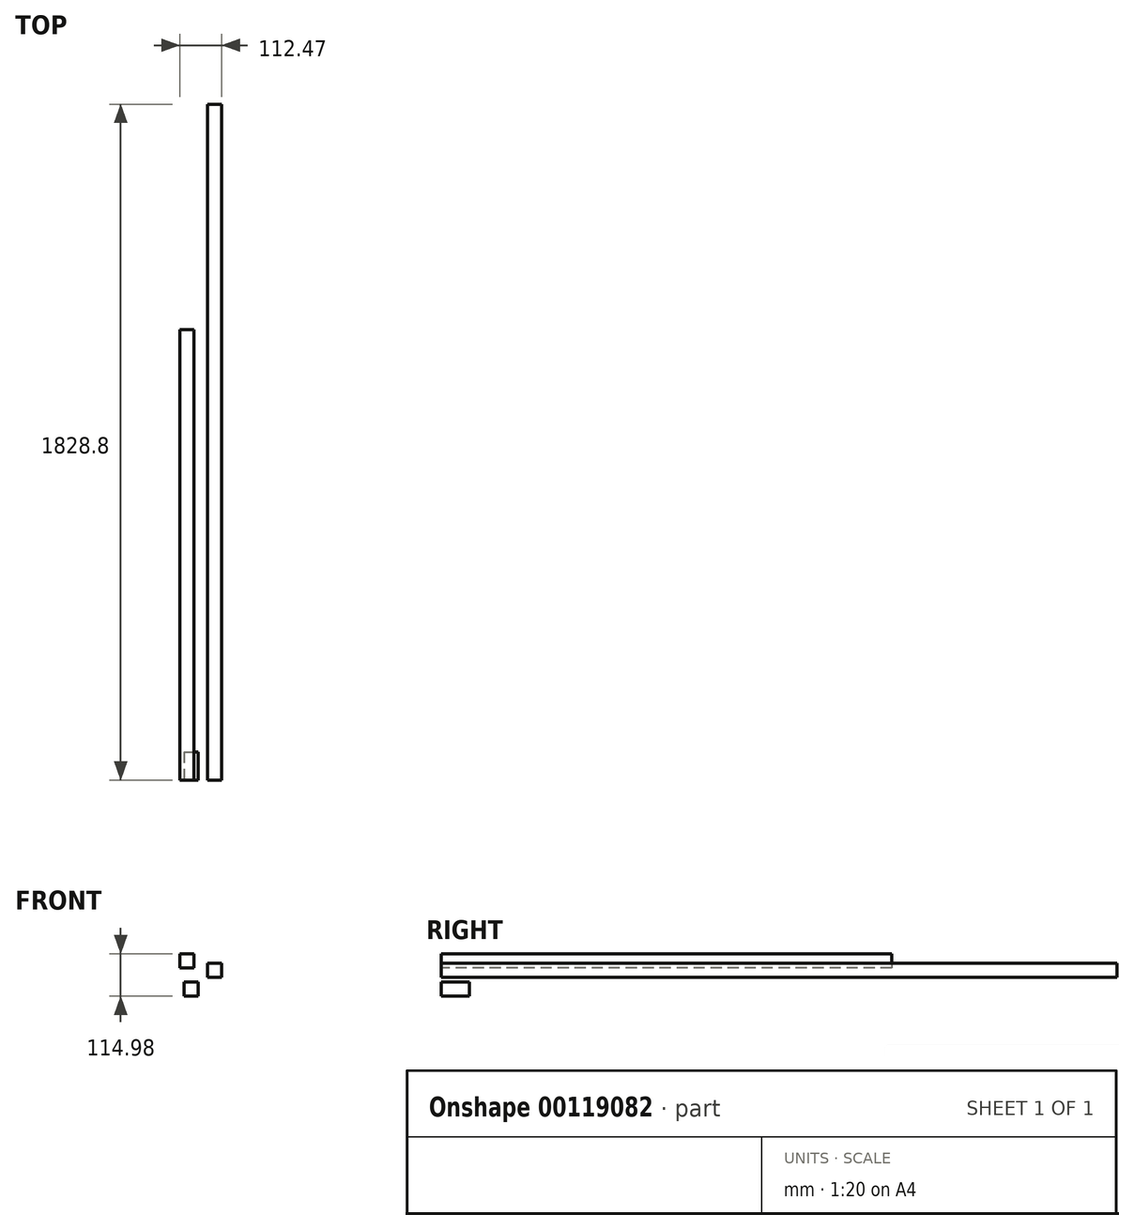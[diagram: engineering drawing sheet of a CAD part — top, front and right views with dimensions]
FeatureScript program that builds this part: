
annotation { "Feature Type Name" : "Feature", "Feature Type Description" : "" }
export const myFeature = defineFeature(function(context is Context, id is Id, definition is map)
    precondition{}
    {
        {
            var Q0;
            Q0=qCreatedBy(makeId("Front.planeOp"),FACE);
            var sketch = newSketch(context, id + "F0", { "sketchPlane" : qUnion([Q0])});
            skLineSegment(sketch, "E0.bottom", {"start": v(0, 0) * mm, "end": v(38.1, 0) * mm});
            skLineSegment(sketch, "E0.top", {"start": v(0, 38.1) * mm, "end": v(38.1, 38.1) * mm});
            skLineSegment(sketch, "E0.left", {"start": v(0, 0) * mm, "end": v(0, 38.1) * mm});
            skLineSegment(sketch, "E0.right", {"start": v(38.1, 0) * mm, "end": v(38.1, 38.1) * mm});
            skSolve(sketch);
        }
        {
            var Q0;
            Q0=makeQuery(id+"F0.imprint","IMPRINT",FACE,{"disambiguationData":[TD([[makeQuery(id+"F0.imprint","IMPRINT",EDGE,{"derivedFrom":sQuery(id+"F0.wireOp",EDGE,"E0.bottom")}),1.0]])]});
            extrude(context, id + "F1", {"entities" : qUnion([Q0]), "oppositeDirection" : true, "depth" : 1828.8 * mm});
        }
        {
            var Q0;
            Q0=qCreatedBy(makeId("Front.planeOp"),FACE);
            var sketch = newSketch(context, id + "F2", { "sketchPlane" : qUnion([Q0])});
            skLineSegment(sketch, "E1.bottom", {"start": v(-74.37, 64.1) * mm, "end": v(-36.27, 64.1) * mm});
            skLineSegment(sketch, "E1.top", {"start": v(-74.37, 26) * mm, "end": v(-36.27, 26) * mm});
            skLineSegment(sketch, "E1.left", {"start": v(-74.37, 64.1) * mm, "end": v(-74.37, 26) * mm});
            skLineSegment(sketch, "E1.right", {"start": v(-36.27, 64.1) * mm, "end": v(-36.27, 26) * mm});
            skLineSegment(sketch, "E2.bottom", {"start": v(-62.35, -12.79) * mm, "end": v(-24.25, -12.79) * mm});
            skLineSegment(sketch, "E2.top", {"start": v(-62.35, -50.89) * mm, "end": v(-24.25, -50.89) * mm});
            skLineSegment(sketch, "E2.left", {"start": v(-62.35, -12.79) * mm, "end": v(-62.35, -50.89) * mm});
            skLineSegment(sketch, "E2.right", {"start": v(-24.25, -12.79) * mm, "end": v(-24.25, -50.89) * mm});
            skSolve(sketch);
        }
        {
            var Q0;
            Q0=makeQuery(id+"F2.imprint","IMPRINT",FACE,{"disambiguationData":[TD([[makeQuery(id+"F2.imprint","IMPRINT",EDGE,{"derivedFrom":sQuery(id+"F2.wireOp",EDGE,"E1.bottom")}),-1.0]])]});
            extrude(context, id + "F3", {"entities" : qUnion([Q0]), "oppositeDirection" : true, "depth" : 1219.2 * mm});
        }
        {
            var Q0;
            Q0=makeQuery(id+"F2.imprint","IMPRINT",FACE,{"disambiguationData":[TD([[makeQuery(id+"F2.imprint","IMPRINT",EDGE,{"derivedFrom":sQuery(id+"F2.wireOp",EDGE,"E2.bottom")}),-1.0]])]});
            extrude(context, id + "F4", {"entities" : qUnion([Q0]), "oppositeDirection" : true, "depth" : 76.2 * mm});
        }
    });
